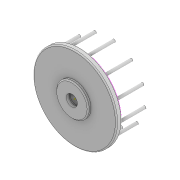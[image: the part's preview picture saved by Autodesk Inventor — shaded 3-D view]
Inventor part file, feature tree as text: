
AUTODESK INVENTOR PART (.ipt)
format: ipt  version: 2021 (Build 250183000, 183)  size: 200,704 bytes
history: native  units: in
note: dims shown in document units (in); Inventor stores cm internally (conversion verified against a paired STEP export)
features: sketch x9, extrude x4, projected_geometry x4, hole x2, chamfer x2, fillet x2
ambient origin geometry x8: Origin, YZ Plane, XZ Plane, XY Plane, X Axis, Y Axis, Z Axis, Center Point
bodies: Solid1 (feature_tree)
feature tree (23):
  sketch  "Sketch1"  dims[d0=5.9055in d1=0.3937in d2=0.0in]
  extrude  "Extrusion1"  Depth=0.3937in TaperAngle=0.0deg
  hole  "Hole1"  [1 undecoded]
  sketch  "Sketch3"  dims[d3=0.1969in d4=0.2362in d5=0.1575in d6=0.0787in d7=90.0deg d8=0.315in d9=0.8108in]
  hole  "Hole2"  [1 undecoded]
  chamfer  "Chamfer1"  Distance=0.1969in
  fillet  "Fillet1"  Radius=0.1969in
  fillet  "Fillet2"  Radius=0.1969in
  extrude  "Extrusion4"  Depth=1.9685in TaperAngle=0.0deg
  chamfer  "Chamfer2"  Distance=1.9685in
  sketch  "Sketch24"  dims[d63=0.0787in d64=0.0787in d65=45.0deg d87=0.1969in d104=0.1969in]
  sketch  "Sketch25"  dims[d105=4.7244in d107=360.0deg d109=1.9685in d110=0.0in]
  sketch  "Sketch26"  dims[d111=0.1969in d112=1.9685in d113=0.0in]
  extrude  "Extrusion6"  Depth=0.8108in
  sketch  "Sketch28"  dims[d19=0.0295in d20=0.8108in]
  extrude  "Extrusion7"  Depth=0.0295in
  sketch  "Sketch4"  dims[d12=0.7874in d13=0.2362in d14=0.1575in d15=0.0787in d16=90.0deg d17=0.315in d18=0.8108in d56=0.0787in d57=0.0787in d58=45.0deg]
  sketch  "Sketch8"  dims[d59=0.0787in d60=0.0787in d61=0.1969in d62=0.0in]
  projected_geometry  "Projected Loop2"
  projected_geometry  "Projected Loop3"
  projected_geometry  "Projected Loop4"
  projected_geometry  "Projected Loop5"
  sketch  "Sketch29"  dims[d21=0.0025in d22=0.0295in d23=0.0148in d43=0.0394in d44=0.0394in d45=0.0394in d46=0.0059in d47=0.0098in d48=0.0148in d49=0.5635in d50=0.0295in d51=0.8108in d52=0.0025in d53=0.0295in d54=0.0148in]
note: 2 required parameter values undecoded (feature->parameter linkage not recoverable at this tier; creation-order binding heuristic only, values carry confidence <= 0.55)
